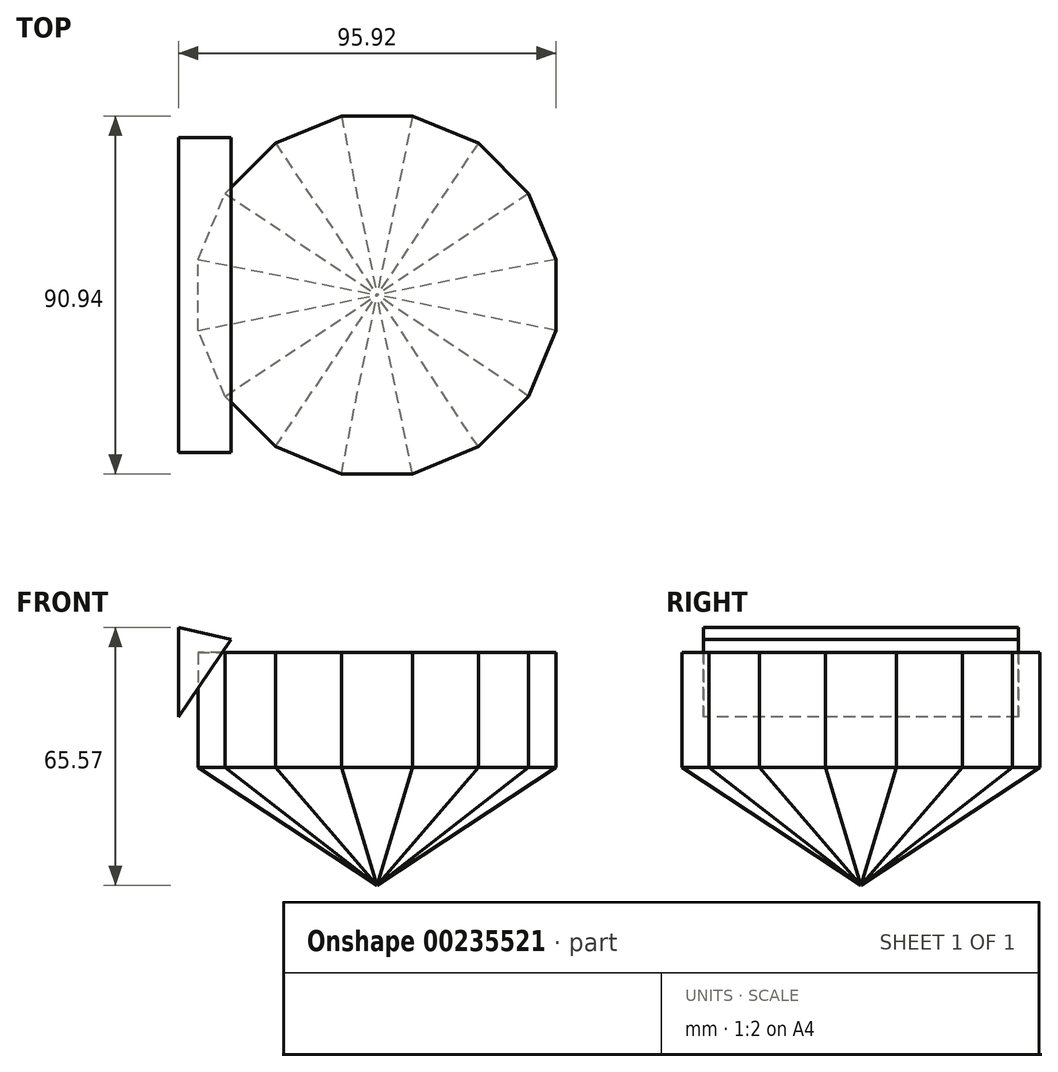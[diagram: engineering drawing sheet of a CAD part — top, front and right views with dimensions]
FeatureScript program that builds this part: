
annotation { "Feature Type Name" : "Feature", "Feature Type Description" : "" }
export const myFeature = defineFeature(function(context is Context, id is Id, definition is map)
    precondition{}
    {
        {
            var Q0;
            Q0=qCreatedBy(makeId("Top.planeOp"),FACE);
            var sketch = newSketch(context, id + "F0", { "sketchPlane" : qUnion([Q0])});
            skCircle(sketch, "E0.cCircle", {"center": v(0, 0) * mm, "radius": 45.47 * mm, "construction": true});
            skLineSegment(sketch, "E0.0", {"start": v(9.04, -45.47) * mm, "end": v(-9.04, -45.47) * mm});
            skLineSegment(sketch, "E0.1", {"start": v(-9.04, -45.47) * mm, "end": v(-25.76, -38.55) * mm});
            skLineSegment(sketch, "E0.2", {"start": v(-25.76, -38.55) * mm, "end": v(-38.55, -25.76) * mm});
            skLineSegment(sketch, "E0.3", {"start": v(-38.55, -25.76) * mm, "end": v(-45.47, -9.04) * mm});
            skLineSegment(sketch, "E0.4", {"start": v(-45.47, -9.04) * mm, "end": v(-45.47, 9.04) * mm});
            skLineSegment(sketch, "E0.5", {"start": v(-45.47, 9.04) * mm, "end": v(-38.55, 25.76) * mm});
            skLineSegment(sketch, "E0.6", {"start": v(-38.55, 25.76) * mm, "end": v(-25.76, 38.55) * mm});
            skLineSegment(sketch, "E0.7", {"start": v(-25.76, 38.55) * mm, "end": v(-9.04, 45.47) * mm});
            skLineSegment(sketch, "E0.8", {"start": v(-9.04, 45.47) * mm, "end": v(9.04, 45.47) * mm});
            skLineSegment(sketch, "E0.9", {"start": v(9.04, 45.47) * mm, "end": v(25.76, 38.55) * mm});
            skLineSegment(sketch, "E0.10", {"start": v(25.76, 38.55) * mm, "end": v(38.55, 25.76) * mm});
            skLineSegment(sketch, "E0.11", {"start": v(38.55, 25.76) * mm, "end": v(45.47, 9.04) * mm});
            skLineSegment(sketch, "E0.12", {"start": v(45.47, 9.04) * mm, "end": v(45.47, -9.04) * mm});
            skLineSegment(sketch, "E0.13", {"start": v(45.47, -9.04) * mm, "end": v(38.55, -25.76) * mm});
            skLineSegment(sketch, "E0.14", {"start": v(38.55, -25.76) * mm, "end": v(25.76, -38.55) * mm});
            skLineSegment(sketch, "E0.15", {"start": v(25.76, -38.55) * mm, "end": v(9.04, -45.47) * mm});
            skPoint(sketch, "E0.0.midPoint", {"position": v(0, -45.47) * mm});
            skSolve(sketch);
        }
        {
            var Q0;
            Q0=qCreatedBy(makeId("Top.planeOp"),FACE);
            cPlane(context, id + "F1", {"entities" : qUnion([Q0]), "cplaneType" : CPlaneType.OFFSET, "offset" : 30 * mm, "oppositeDirection" : true, "width" : 150 * mm, "height" : 150 * mm});
        }
        {
            var Q0;
            Q0=qCreatedBy(id+"F1.planeOp",FACE);
            var sketch = newSketch(context, id + "F2", { "sketchPlane" : qUnion([Q0])});
            skPoint(sketch, "E1", {"position": v(0, 0) * mm});
            skSolve(sketch);
        }
        {
            var Q0;
            Q0=makeQuery(id+"F0.imprint","IMPRINT",FACE,{"disambiguationData":[TD([[makeQuery(id+"F0.imprint","IMPRINT",EDGE,{"derivedFrom":sQuery(id+"F0.wireOp",EDGE,"E0.0")}),-1.0]])]});
            var Q1;
            Q1=sQuery(id+"F2.wireOp",VERTEX,"E1");
            loft(context, id + "F3", {"sheetProfilesArray" : [{ "sheetProfileEntities" : qUnion([Q0]) }, { "sheetProfileEntities" : qUnion([Q1]) }]});
        }
        {
            var Q0;
            Q0=makeQuery(id+"F3.opLoft","CAP_FACE",FACE,{"disambiguationData":[OSD([makeQuery(id+"F0.imprint","IMPRINT",FACE,{"disambiguationData":[TD([[makeQuery(id+"F0.imprint","IMPRINT",EDGE,{"derivedFrom":sQuery(id+"F0.wireOp",EDGE,"E0.0")}),-1.0]])]})])],"isStart":true});
            extrude(context, id + "F4", {"entities" : qUnion([Q0]), "operationType" : NewBodyOperationType.ADD, "depth" : 29.2 * mm});
        }
        {
            var Q0;
            Q0=qCreatedBy(makeId("Front.planeOp"),FACE);
            var sketch = newSketch(context, id + "F5", { "sketchPlane" : qUnion([Q0])});
            skLineSegment(sketch, "E2", {"start": v(-37.06, 32.52) * mm, "end": v(-50.45, 12.8) * mm});
            skLineSegment(sketch, "E3", {"start": v(-50.45, 12.8) * mm, "end": v(-50.45, 35.57) * mm});
            skLineSegment(sketch, "E4", {"start": v(-50.45, 35.57) * mm, "end": v(-37.06, 32.52) * mm});
            skSolve(sketch);
        }
        {
            var Q0;
            Q0=makeQuery(id+"F5.imprint","IMPRINT",FACE,{"disambiguationData":[TD([[makeQuery(id+"F5.imprint","IMPRINT",EDGE,{"derivedFrom":sQuery(id+"F5.wireOp",EDGE,"E2")}),-1.0]])]});
            extrude(context, id + "F6", {"entities" : qUnion([Q0]), "endBound" : BoundingType.SYMMETRIC, "oppositeDirection" : true, "depth" : 80 * mm});
        }
    });
